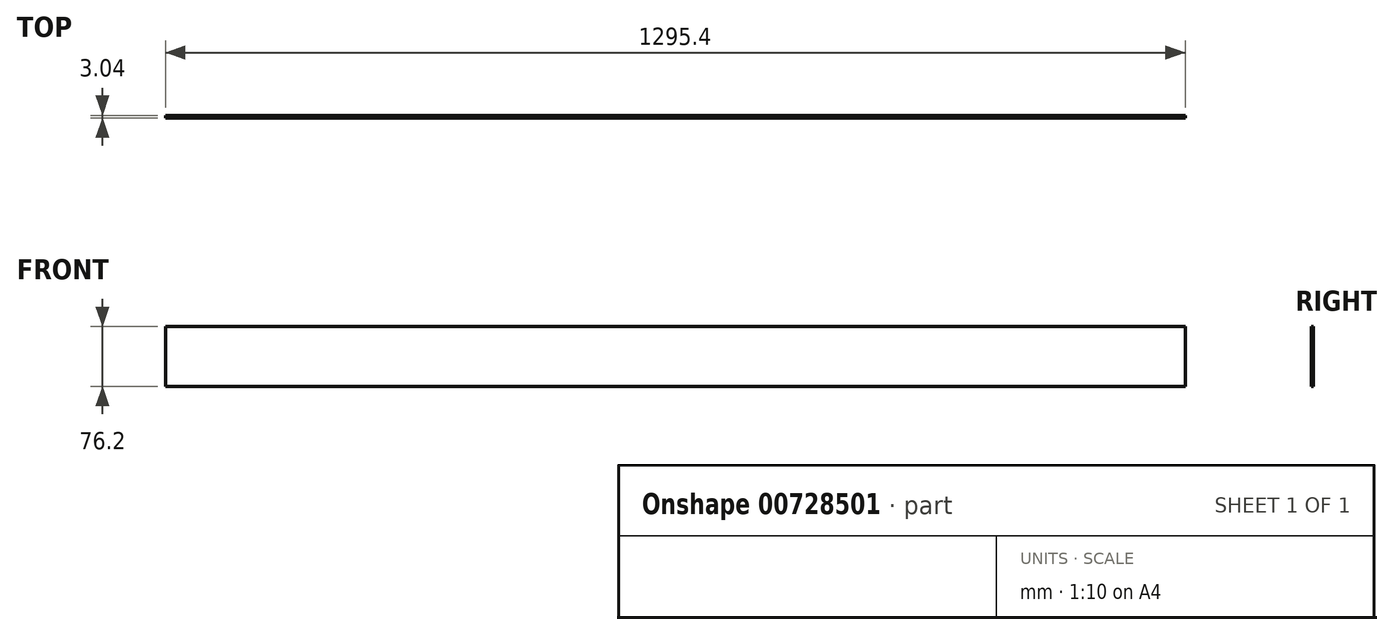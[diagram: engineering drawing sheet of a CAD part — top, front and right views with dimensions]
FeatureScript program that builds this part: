
annotation { "Feature Type Name" : "Feature", "Feature Type Description" : "" }
export const myFeature = defineFeature(function(context is Context, id is Id, definition is map)
    precondition{}
    {
        {
            var Q0;
            Q0=qCreatedBy(makeId("Front.planeOp"),FACE);
            var sketch = newSketch(context, id + "F0", { "sketchPlane" : qUnion([Q0])});
            skLineSegment(sketch, "E0.bottom", {"start": v(-647.7, 38.1) * mm, "end": v(647.7, 38.1) * mm});
            skLineSegment(sketch, "E0.top", {"start": v(-647.7, -38.1) * mm, "end": v(647.7, -38.1) * mm});
            skLineSegment(sketch, "E0.left", {"start": v(-647.7, 38.1) * mm, "end": v(-647.7, -38.1) * mm});
            skLineSegment(sketch, "E0.right", {"start": v(647.7, 38.1) * mm, "end": v(647.7, -38.1) * mm});
            skPoint(sketch, "E0.middle", {"position": v(0, 0) * mm});
            skSolve(sketch);
        }
        {
            var Q0;
            Q0=makeQuery(id+"F0.imprint","IMPRINT",FACE,{"disambiguationData":[TD([[makeQuery(id+"F0.imprint","IMPRINT",EDGE,{"derivedFrom":sQuery(id+"F0.wireOp",EDGE,"E0.bottom")}),-1.0]])]});
            extrude(context, id + "F1", {"entities" : qUnion([Q0]), "endBound" : BoundingType.SYMMETRIC, "depth" : 3.05 * mm, "offsetDistance" : 25.4 * mm});
        }
    });
